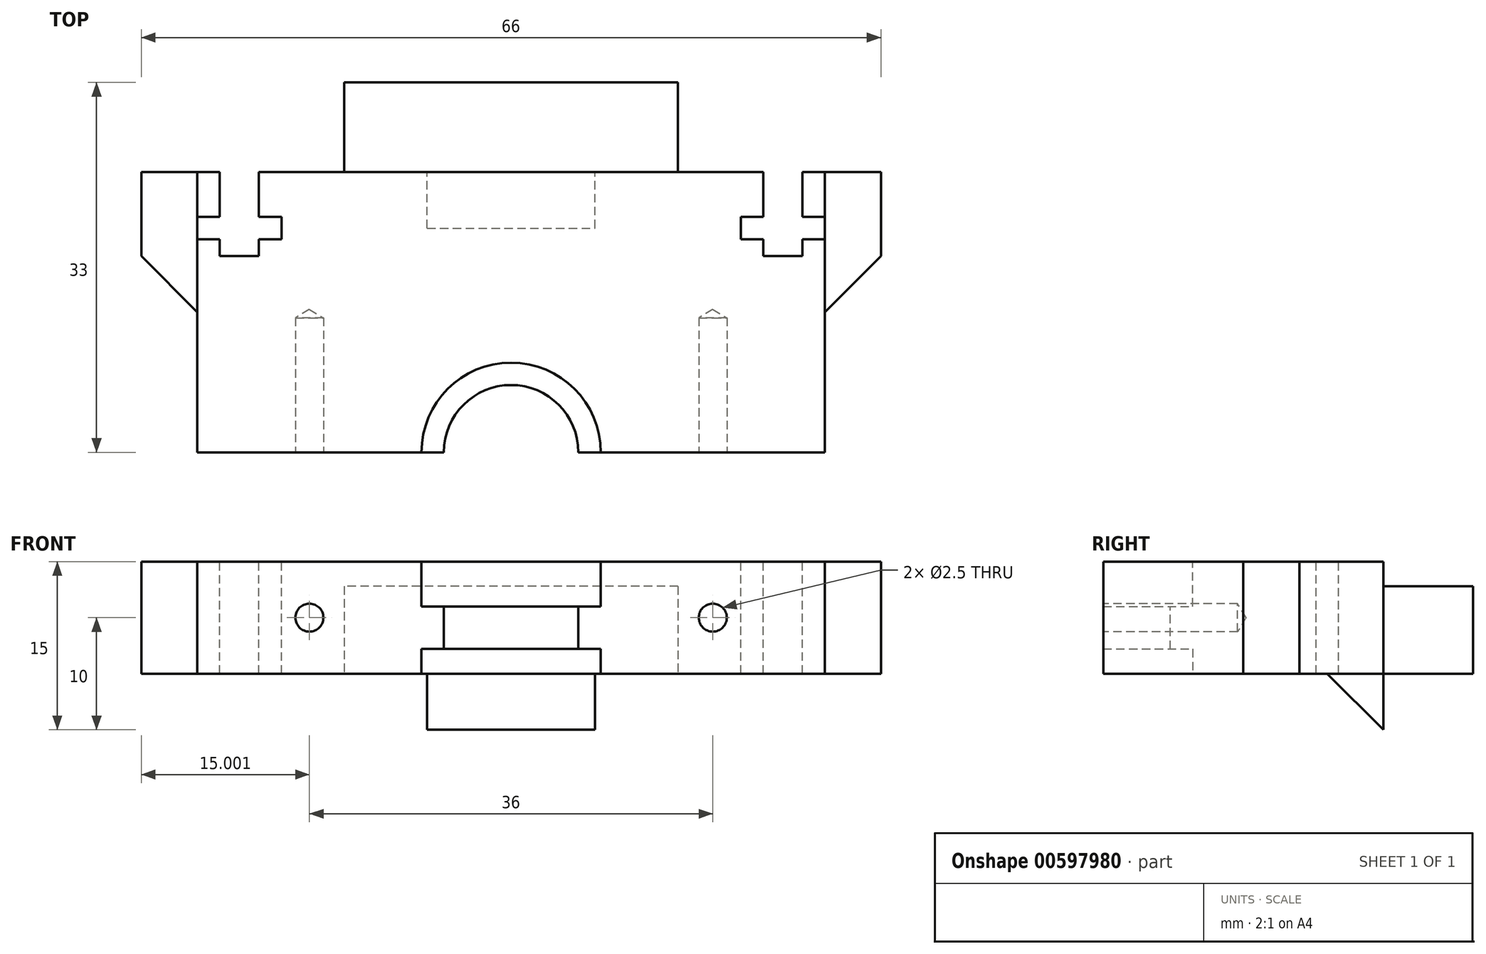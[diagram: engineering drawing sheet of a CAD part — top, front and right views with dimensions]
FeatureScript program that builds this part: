
annotation { "Feature Type Name" : "Feature", "Feature Type Description" : "" }
export const myFeature = defineFeature(function(context is Context, id is Id, definition is map)
    precondition{}
    {
        {
            var Q0;
            Q0=qCreatedBy(makeId("Top.planeOp"),FACE);
            var sketch = newSketch(context, id + "F0", { "sketchPlane" : qUnion([Q0])});
            skLineSegment(sketch, "E0.bottom", {"start": v(-25.38, 11.36) * mm, "end": v(30.62, 11.36) * mm});
            skLineSegment(sketch, "E0.top", {"start": v(-25.38, -13.64) * mm, "end": v(30.62, -13.64) * mm});
            skLineSegment(sketch, "E0.left", {"start": v(-25.38, 11.36) * mm, "end": v(-25.38, -13.64) * mm});
            skLineSegment(sketch, "E0.right", {"start": v(30.62, 11.36) * mm, "end": v(30.62, -13.64) * mm});
            skSolve(sketch);
        }
        {
            var Q0;
            Q0 = qSketchRegion(id + "F0", true);
            extrude(context, id + "F1", {"entities" : qUnion([Q0]), "depth" : 10 * mm, "offsetDistance" : 25 * mm});
        }
        {
            var Q0;
            Q0=makeQuery(id+"F1.opExtrude","CAP_FACE",FACE,{"disambiguationData":[OSD([sQuery(id+"F0.wireOp",EDGE,"E0.bottom"),sQuery(id+"F0.wireOp",EDGE,"E0.top"),sQuery(id+"F0.wireOp",EDGE,"E0.left"),sQuery(id+"F0.wireOp",EDGE,"E0.right")])],"isStart":false});
            var sketch = newSketch(context, id + "F2", { "sketchPlane" : qUnion([Q0])});
            skLineSegment(sketch, "E1", {"start": v(28.62, 11.36) * mm, "end": v(28.62, 7.36) * mm});
            skLineSegment(sketch, "E2", {"start": v(28.62, 7.36) * mm, "end": v(30.62, 7.36) * mm});
            skLineSegment(sketch, "E3", {"start": v(30.62, 7.36) * mm, "end": v(30.62, 5.36) * mm});
            skLineSegment(sketch, "E4", {"start": v(30.62, 5.36) * mm, "end": v(28.62, 5.36) * mm});
            skLineSegment(sketch, "E5", {"start": v(28.62, 5.36) * mm, "end": v(28.62, 3.86) * mm});
            skLineSegment(sketch, "E6", {"start": v(28.62, 3.86) * mm, "end": v(25.12, 3.86) * mm});
            skLineSegment(sketch, "E7", {"start": v(25.12, 3.86) * mm, "end": v(25.12, 5.36) * mm});
            skLineSegment(sketch, "E8", {"start": v(25.12, 5.36) * mm, "end": v(23.12, 5.36) * mm});
            skLineSegment(sketch, "E9", {"start": v(23.12, 5.36) * mm, "end": v(23.12, 7.36) * mm});
            skLineSegment(sketch, "E10", {"start": v(23.12, 7.36) * mm, "end": v(25.12, 7.36) * mm});
            skLineSegment(sketch, "E11", {"start": v(25.12, 7.36) * mm, "end": v(25.12, 11.36) * mm});
            skLineSegment(sketch, "E12", {"start": v(25.12, 11.36) * mm, "end": v(28.62, 11.36) * mm});
            skSolve(sketch);
        }
        {
            var Q0;
            Q0 = qSketchRegion(id + "F2", true);
            extrude(context, id + "F3", {"entities" : qUnion([Q0]), "operationType" : NewBodyOperationType.REMOVE, "oppositeDirection" : true, "depth" : 25 * mm, "offsetDistance" : 25 * mm});
        }
        {
            var Q0;
            Q0=makeQuery(id+"F1.opExtrude","CAP_FACE",FACE,{"disambiguationData":[OSD([sQuery(id+"F0.wireOp",EDGE,"E0.bottom"),sQuery(id+"F0.wireOp",EDGE,"E0.top"),sQuery(id+"F0.wireOp",EDGE,"E0.left"),sQuery(id+"F0.wireOp",EDGE,"E0.right")])],"isStart":false});
            var sketch = newSketch(context, id + "F4", { "sketchPlane" : qUnion([Q0])});
            skLineSegment(sketch, "E13", {"start": v(-19.88, 11.36) * mm, "end": v(-19.88, 7.36) * mm});
            skLineSegment(sketch, "E14", {"start": v(-19.88, 7.36) * mm, "end": v(-17.88, 7.36) * mm});
            skLineSegment(sketch, "E15", {"start": v(-17.88, 7.36) * mm, "end": v(-17.88, 5.36) * mm});
            skLineSegment(sketch, "E16", {"start": v(-17.88, 5.36) * mm, "end": v(-19.88, 5.36) * mm});
            skLineSegment(sketch, "E17", {"start": v(-19.88, 5.36) * mm, "end": v(-19.88, 3.86) * mm});
            skLineSegment(sketch, "E18", {"start": v(-19.88, 3.86) * mm, "end": v(-23.38, 3.86) * mm});
            skLineSegment(sketch, "E19", {"start": v(-23.38, 3.86) * mm, "end": v(-23.38, 5.36) * mm});
            skLineSegment(sketch, "E20", {"start": v(-23.38, 5.36) * mm, "end": v(-25.38, 5.36) * mm});
            skLineSegment(sketch, "E21", {"start": v(-25.38, 5.36) * mm, "end": v(-25.38, 7.36) * mm});
            skLineSegment(sketch, "E22", {"start": v(-25.38, 7.36) * mm, "end": v(-23.38, 7.36) * mm});
            skLineSegment(sketch, "E23", {"start": v(-23.38, 7.36) * mm, "end": v(-23.38, 11.36) * mm});
            skLineSegment(sketch, "E24", {"start": v(-23.38, 11.36) * mm, "end": v(-19.88, 11.36) * mm});
            skSolve(sketch);
        }
        {
            var Q0;
            Q0 = qSketchRegion(id + "F4", true);
            extrude(context, id + "F5", {"entities" : qUnion([Q0]), "operationType" : NewBodyOperationType.REMOVE, "oppositeDirection" : true, "depth" : 25 * mm, "offsetDistance" : 25 * mm});
        }
        {
            var Q0;
            Q0=makeQuery(id+"F1.opExtrude","CAP_FACE",FACE,{"disambiguationData":[OSD([sQuery(id+"F0.wireOp",EDGE,"E0.bottom"),sQuery(id+"F0.wireOp",EDGE,"E0.top"),sQuery(id+"F0.wireOp",EDGE,"E0.left"),sQuery(id+"F0.wireOp",EDGE,"E0.right")])],"isStart":false});
            var sketch = newSketch(context, id + "F6", { "sketchPlane" : qUnion([Q0])});
            skCircle(sketch, "E25", {"center": v(2.62, -13.64) * mm, "radius": 6 * mm});
            skSolve(sketch);
        }
        {
            var Q0;
            Q0 = qSketchRegion(id + "F6", true);
            extrude(context, id + "F7", {"entities" : qUnion([Q0]), "operationType" : NewBodyOperationType.REMOVE, "oppositeDirection" : true, "depth" : 25 * mm, "offsetDistance" : 25 * mm});
        }
        {
            var Q0;
            Q0=makeQuery(id+"F1.opExtrude","CAP_FACE",FACE,{"disambiguationData":[OSD([sQuery(id+"F0.wireOp",EDGE,"E0.bottom"),sQuery(id+"F0.wireOp",EDGE,"E0.top"),sQuery(id+"F0.wireOp",EDGE,"E0.left"),sQuery(id+"F0.wireOp",EDGE,"E0.right")])],"isStart":false});
            var sketch = newSketch(context, id + "F8", { "sketchPlane" : qUnion([Q0])});
            skCircle(sketch, "E26", {"center": v(2.62, -13.64) * mm, "radius": 8 * mm});
            skSolve(sketch);
        }
        {
            var Q0;
            Q0 = qSketchRegion(id + "F8", true);
            extrude(context, id + "F9", {"entities" : qUnion([Q0]), "operationType" : NewBodyOperationType.REMOVE, "oppositeDirection" : true, "depth" : 4 * mm, "offsetDistance" : 25 * mm});
        }
        {
            var Q0;
            Q0=makeQuery(id+"F1.opExtrude","CAP_FACE",FACE,{"disambiguationData":[OSD([sQuery(id+"F0.wireOp",EDGE,"E0.bottom"),sQuery(id+"F0.wireOp",EDGE,"E0.top"),sQuery(id+"F0.wireOp",EDGE,"E0.left"),sQuery(id+"F0.wireOp",EDGE,"E0.right")])],"isStart":true});
            var sketch = newSketch(context, id + "F10", { "sketchPlane" : qUnion([Q0])});
            skCircle(sketch, "E27", {"center": v(2.62, 13.64) * mm, "radius": 8 * mm});
            skSolve(sketch);
        }
        {
            var Q0;
            Q0 = qSketchRegion(id + "F10", true);
            extrude(context, id + "F11", {"entities" : qUnion([Q0]), "operationType" : NewBodyOperationType.REMOVE, "oppositeDirection" : true, "depth" : 2.2 * mm, "offsetDistance" : 25 * mm});
        }
        {
            var Q0;
            {var subQ0=sQuery(id+"F0.wireOp",EDGE,"E0.right");var subQ2=sQuery(id+"F0.wireOp",EDGE,"E0.top");Q0=makeQuery(id+"F7.boolean.opBoolean","SPLIT",FACE,{"disambiguationData":[TD([makeQuery(id+"F1.opExtrude","SWEPT_FACE",FACE,{"disambiguationData":[OSD([subQ0])]})])],"derivedFrom":makeQuery(id+"F1.opExtrude","SWEPT_FACE",FACE,{"disambiguationData":[OSD([subQ2])]})});}
            var sketch = newSketch(context, id + "F12", { "sketchPlane" : qUnion([Q0])});
            skPoint(sketch, "E28", {"position": v(20.62, 5) * mm});
            skPoint(sketch, "E29", {"position": v(-15.38, 5) * mm});
            skSolve(sketch);
        }
        {
            var Q0;
            Q0=sQuery(id+"F12.wireOp",VERTEX,"E29");
            var Q1;
            Q1=sQuery(id+"F12.wireOp",VERTEX,"E28");
            var Q2;
            Q2=makeQuery(id+"F1.opExtrude","SWEPT_BODY",BODY,{"disambiguationData":[OSD([sQuery(id+"F0.wireOp",EDGE,"E0.bottom"),sQuery(id+"F0.wireOp",EDGE,"E0.top"),sQuery(id+"F0.wireOp",EDGE,"E0.left"),sQuery(id+"F0.wireOp",EDGE,"E0.right")])]});
            hole(context, id + "F13", {"style" : HoleStyle.SIMPLE, "endStyle" : HoleEndStyle.BLIND, "holeDiameter" : 2.5 * mm, "majorDiameter" : 5 * mm, "holeDepth" : 12 * mm, "isTappedThrough" : true, "tappedDepth" : 12 * mm, "tapClearance" : 3, "locations" : qUnion([Q0, Q1]), "scope" : qUnion([Q2])});
        }
        {
            var Q0;
            Q0=makeQuery(id+"F1.opExtrude","CAP_FACE",FACE,{"disambiguationData":[OSD([sQuery(id+"F0.wireOp",EDGE,"E0.bottom"),sQuery(id+"F0.wireOp",EDGE,"E0.top"),sQuery(id+"F0.wireOp",EDGE,"E0.left"),sQuery(id+"F0.wireOp",EDGE,"E0.right")])],"isStart":true});
            var sketch = newSketch(context, id + "F14", { "sketchPlane" : qUnion([Q0])});
            skLineSegment(sketch, "E30.bottom", {"start": v(-4.88, -6.36) * mm, "end": v(10.12, -6.36) * mm});
            skLineSegment(sketch, "E30.top", {"start": v(-4.88, -11.36) * mm, "end": v(10.12, -11.36) * mm});
            skLineSegment(sketch, "E30.left", {"start": v(-4.88, -6.36) * mm, "end": v(-4.88, -11.36) * mm});
            skLineSegment(sketch, "E30.right", {"start": v(10.12, -6.36) * mm, "end": v(10.12, -11.36) * mm});
            skSolve(sketch);
        }
        {
            var Q0;
            Q0 = qSketchRegion(id + "F14", true);
            extrude(context, id + "F15", {"entities" : qUnion([Q0]), "operationType" : NewBodyOperationType.ADD, "depth" : 5 * mm, "offsetDistance" : 25 * mm});
        }
        {
            var Q0;
            Q0=makeQuery(id+"F15.opExtrude","CAP_EDGE",EDGE,{"disambiguationData":[OSD([sQuery(id+"F14.wireOp",EDGE,"E30.bottom")])],"isStart":false});
            chamfer(context, id + "F16", {"entities" : qUnion([Q0]), "width" : 5 * mm, "tangentPropagation" : true});
        }
        {
            var Q0;
            {var subQ0=sQuery(id+"F0.wireOp",EDGE,"E0.left");var subQ1=sQuery(id+"F0.wireOp",EDGE,"E0.top");var subQ2=sQuery(id+"F0.wireOp",EDGE,"E0.right");var subQ3=sQuery(id+"F0.wireOp",EDGE,"E0.bottom");Q0=makeQuery(id+"F5.boolean.opBoolean","SPLIT",FACE,{"disambiguationData":[TD([makeQuery(id+"F1.opExtrude","SWEPT_FACE",FACE,{"disambiguationData":[OSD([subQ1])]})])],"derivedFrom":makeQuery(id+"F1.opExtrude","CAP_FACE",FACE,{"disambiguationData":[OSD([subQ3,subQ1,subQ0,subQ2])],"isStart":false})});}
            var sketch = newSketch(context, id + "F17", { "sketchPlane" : qUnion([Q0])});
            skLineSegment(sketch, "E31.bottom", {"start": v(-25.38, -1.14) * mm, "end": v(-30.38, -1.14) * mm});
            skLineSegment(sketch, "E31.top", {"start": v(-25.38, 11.36) * mm, "end": v(-30.38, 11.36) * mm});
            skLineSegment(sketch, "E31.left", {"start": v(-25.38, -1.14) * mm, "end": v(-25.38, 11.36) * mm});
            skLineSegment(sketch, "E31.right", {"start": v(-30.38, -1.14) * mm, "end": v(-30.38, 11.36) * mm});
            skLineSegment(sketch, "E32.bottom", {"start": v(30.62, -1.14) * mm, "end": v(35.62, -1.14) * mm});
            skLineSegment(sketch, "E32.top", {"start": v(30.62, 11.36) * mm, "end": v(35.62, 11.36) * mm});
            skLineSegment(sketch, "E32.left", {"start": v(30.62, -1.14) * mm, "end": v(30.62, 11.36) * mm});
            skLineSegment(sketch, "E32.right", {"start": v(35.62, -1.14) * mm, "end": v(35.62, 11.36) * mm});
            skSolve(sketch);
        }
        {
            var Q0;
            Q0 = qSketchRegion(id + "F17", true);
            extrude(context, id + "F18", {"entities" : qUnion([Q0]), "oppositeDirection" : true, "depth" : 10 * mm, "offsetDistance" : 25 * mm});
        }
        {
            var Q0;
            Q0=makeQuery(id+"F18.opExtrude","SWEPT_EDGE",EDGE,{"disambiguationData":[OSD([sQuery(id+"F17.wireOp",EDGE,"E32.bottom"),sQuery(id+"F17.wireOp",EDGE,"E32.right")])]});
            var Q1;
            Q1=makeQuery(id+"F18.opExtrude","SWEPT_EDGE",EDGE,{"disambiguationData":[OSD([sQuery(id+"F17.wireOp",EDGE,"E31.bottom"),sQuery(id+"F17.wireOp",EDGE,"E31.right")])]});
            chamfer(context, id + "F19", {"entities" : qUnion([Q0, Q1]), "width" : 5 * mm, "tangentPropagation" : true});
        }
        {
            var Q0;
            {var subQ1=sQuery(id+"F0.wireOp",EDGE,"E0.left");var subQ3=sQuery(id+"F0.wireOp",EDGE,"E0.bottom");var subQ6=makeQuery(id+"F3.opExtrude","SWEPT_FACE",FACE,{"disambiguationData":[OSD([sQuery(id+"F2.wireOp",EDGE,"E11")])]});Q0=makeQuery(id+"F15.boolean.opBoolean","MERGE",FACE,{"derivedFrom":[makeQuery(id+"F5.boolean.opBoolean","SPLIT",FACE,{"disambiguationData":[TD([makeQuery(id+"F3.boolean.opBoolean","COPY",FACE,{"derivedFrom":subQ6})])],"derivedFrom":makeQuery(id+"F3.boolean.opBoolean","SPLIT",FACE,{"disambiguationData":[TD([makeQuery(id+"F1.opExtrude","SWEPT_FACE",FACE,{"disambiguationData":[OSD([subQ1])]})])],"derivedFrom":makeQuery(id+"F1.opExtrude","SWEPT_FACE",FACE,{"disambiguationData":[OSD([subQ3])]})})}),makeQuery(id+"F15.opExtrude","SWEPT_FACE",FACE,{"disambiguationData":[OSD([sQuery(id+"F14.wireOp",EDGE,"E30.top")])]})]});}
            var sketch = newSketch(context, id + "F20", { "sketchPlane" : qUnion([Q0])});
            skLineSegment(sketch, "E33.bottom", {"start": v(-17.52, 7.8) * mm, "end": v(12.28, 7.8) * mm});
            skLineSegment(sketch, "E33.top", {"start": v(-17.52, 0) * mm, "end": v(12.28, 0) * mm});
            skLineSegment(sketch, "E33.left", {"start": v(-17.52, 7.8) * mm, "end": v(-17.52, 0) * mm});
            skLineSegment(sketch, "E33.right", {"start": v(12.28, 7.8) * mm, "end": v(12.28, 0) * mm});
            skSolve(sketch);
        }
        {
            var Q0;
            Q0 = qSketchRegion(id + "F20", true);
            extrude(context, id + "F21", {"entities" : qUnion([Q0]), "operationType" : NewBodyOperationType.ADD, "depth" : 8 * mm, "offsetDistance" : 25 * mm});
        }
    });
